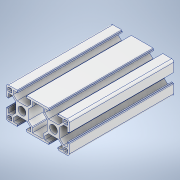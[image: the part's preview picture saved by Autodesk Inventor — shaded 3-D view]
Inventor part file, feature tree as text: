
AUTODESK INVENTOR PART (.ipt)
format: ipt  version: 2020 (Build 240168000, 168)  size: 297,984 bytes
history: native  units: mm
features: extrude x1, sketch x1
ambient origin geometry x8: Origin, YZ Plane, XZ Plane, XY Plane, X Axis, Y Axis, Z Axis, Center Point
bodies: Solid1 (feature_tree)
feature tree (2):
  extrude  "Extrusion1"  [1 undecoded]
  sketch  "Sketch1"  dims[d0=99.5mm d1=0.0mm]
note: 1 required parameter value undecoded (feature->parameter linkage not recoverable at this tier; creation-order binding heuristic only, values carry confidence <= 0.55)
